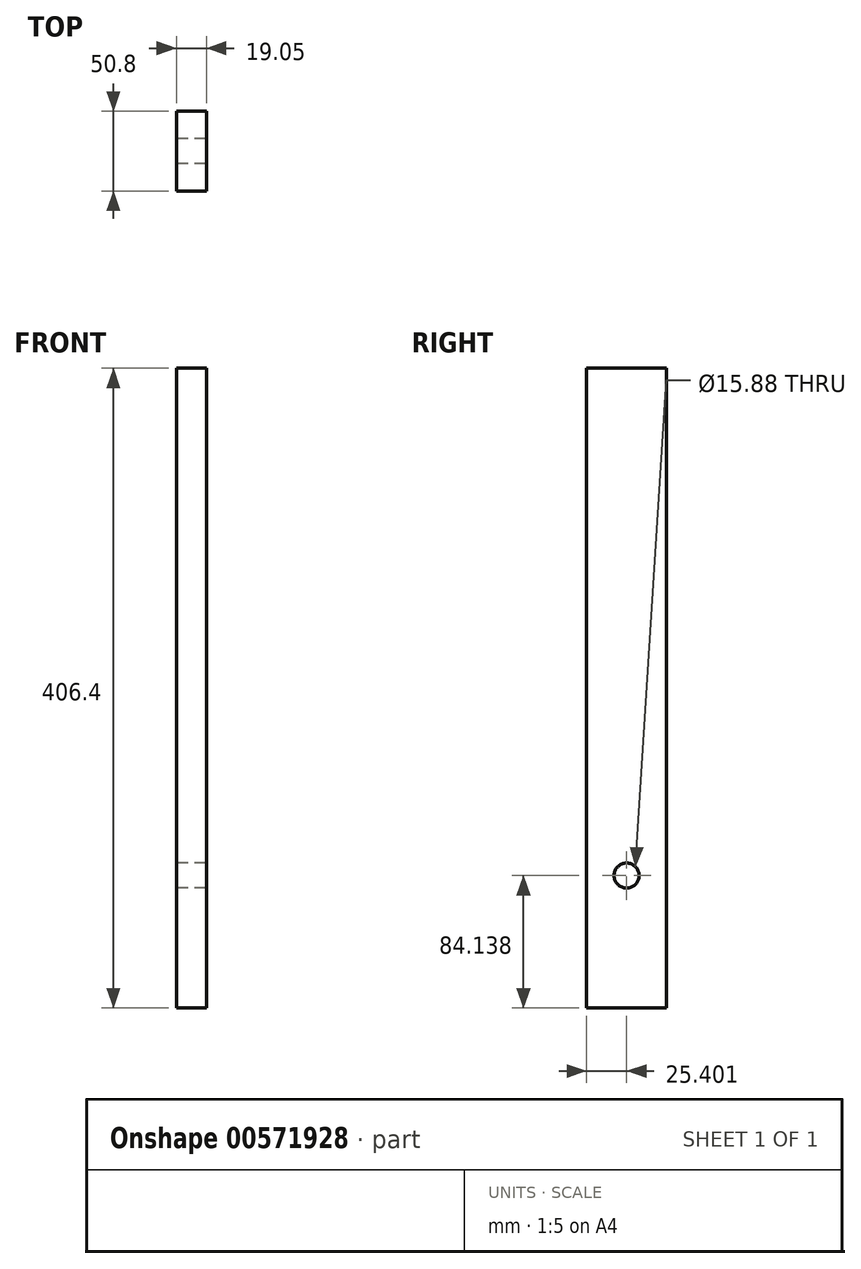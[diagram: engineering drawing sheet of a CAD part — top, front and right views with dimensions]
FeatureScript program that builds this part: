
annotation { "Feature Type Name" : "Feature", "Feature Type Description" : "" }
export const myFeature = defineFeature(function(context is Context, id is Id, definition is map)
    precondition{}
    {
        {
            var Q0;
            Q0=qCreatedBy(makeId("Top.planeOp"),FACE);
            var sketch = newSketch(context, id + "F0", { "sketchPlane" : qUnion([Q0])});
            skLineSegment(sketch, "E0.bottom", {"start": v(-37.34, -16.55) * mm, "end": v(-88.14, -16.55) * mm});
            skLineSegment(sketch, "E0.top", {"start": v(-37.34, -67.35) * mm, "end": v(-88.14, -67.35) * mm});
            skLineSegment(sketch, "E0.left", {"start": v(-37.34, -16.55) * mm, "end": v(-37.34, -67.35) * mm});
            skLineSegment(sketch, "E0.right", {"start": v(-88.14, -16.55) * mm, "end": v(-88.14, -67.35) * mm});
            skSolve(sketch);
        }
        {
            var Q0;
            Q0 = qSketchRegion(id + "F0", true);
            extrude(context, id + "F1", {"entities" : qUnion([Q0]), "depth" : 406.4 * mm, "offsetDistance" : 25.4 * mm});
        }
        {
            var Q0;
            Q0=makeQuery(id+"F1.opExtrude","SWEPT_FACE",FACE,{"disambiguationData":[OSD([sQuery(id+"F0.wireOp",EDGE,"E0.left")])]});
            extrude(context, id + "F2", {"entities" : qUnion([Q0]), "operationType" : NewBodyOperationType.REMOVE, "oppositeDirection" : true, "depth" : 31.75 * mm, "offsetDistance" : 25.4 * mm});
        }
        {
            var Q0;
            Q0=makeQuery(id+"F1.opExtrude","SWEPT_FACE",FACE,{"disambiguationData":[OSD([sQuery(id+"F0.wireOp",EDGE,"E0.right")])]});
            var sketch = newSketch(context, id + "F3", { "sketchPlane" : qUnion([Q0])});
            skCircle(sketch, "E1", {"center": v(41.95, 84.14) * mm, "radius": 7.94 * mm});
            skSolve(sketch);
        }
        {
            var Q0;
            Q0=makeQuery(id+"F3.imprint","IMPRINT",FACE,{"disambiguationData":[TD([[makeQuery(id+"F3.imprint","IMPRINT",EDGE,{"derivedFrom":sQuery(id+"F3.wireOp",EDGE,"E1")}),1.0]])]});
            extrude(context, id + "F4", {"entities" : qUnion([Q0]), "operationType" : NewBodyOperationType.REMOVE, "oppositeDirection" : true, "depth" : 19.05 * mm, "offsetDistance" : 25.4 * mm});
        }
    });
